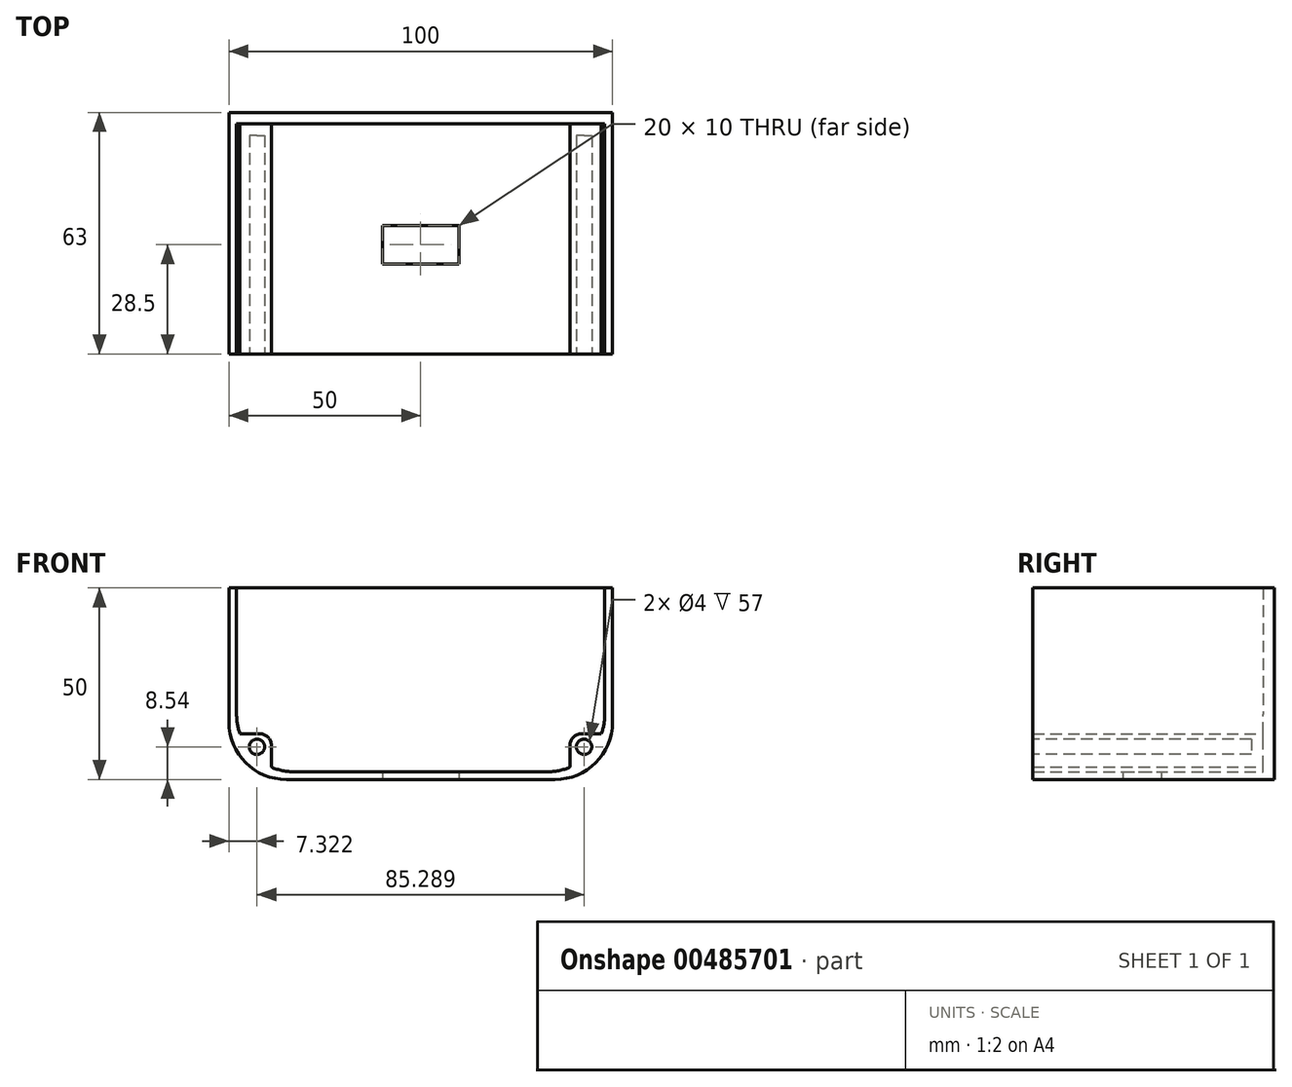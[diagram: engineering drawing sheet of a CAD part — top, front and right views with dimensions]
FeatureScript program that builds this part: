
annotation { "Feature Type Name" : "Feature", "Feature Type Description" : "" }
export const myFeature = defineFeature(function(context is Context, id is Id, definition is map)
    precondition{}
    {
        {
            var Q0;
            Q0=qCreatedBy(makeId("Front.planeOp"),FACE);
            var sketch = newSketch(context, id + "F0", { "sketchPlane" : qUnion([Q0])});
            skLineSegment(sketch, "E0.bottom", {"start": v(0, 0) * mm, "end": v(100, 0) * mm});
            skLineSegment(sketch, "E0.top", {"start": v(0, 50) * mm, "end": v(100, 50) * mm});
            skLineSegment(sketch, "E0.left", {"start": v(0, 0) * mm, "end": v(0, 50) * mm});
            skLineSegment(sketch, "E0.right", {"start": v(100, 0) * mm, "end": v(100, 50) * mm});
            skLineSegment(sketch, "E1.0", {"start": v(2, 2) * mm, "end": v(2, 48) * mm});
            skLineSegment(sketch, "E1.1", {"start": v(2, 2) * mm, "end": v(98, 2) * mm});
            skLineSegment(sketch, "E1.2", {"start": v(98, 2) * mm, "end": v(98, 48) * mm});
            skLineSegment(sketch, "E1.3", {"start": v(2, 48) * mm, "end": v(98, 48) * mm});
            skSolve(sketch);
        }
        {
            var Q0;
            Q0 = qSketchRegion(id + "F0", true);
            extrude(context, id + "F1", {"entities" : qUnion([Q0]), "depth" : 65 * mm, "offsetDistance" : 25 * mm});
        }
        {
            var Q0;
            Q0=makeQuery(id+"F1.opExtrude","CAP_FACE",FACE,{"disambiguationData":[OSD([sQuery(id+"F0.wireOp",EDGE,"E0.bottom"),sQuery(id+"F0.wireOp",EDGE,"E0.top"),sQuery(id+"F0.wireOp",EDGE,"E0.left"),sQuery(id+"F0.wireOp",EDGE,"E0.right"),sQuery(id+"F0.wireOp",EDGE,"E1.0"),sQuery(id+"F0.wireOp",EDGE,"E1.1"),sQuery(id+"F0.wireOp",EDGE,"E1.2"),sQuery(id+"F0.wireOp",EDGE,"E1.3")])],"isStart":false});
            var sketch = newSketch(context, id + "F2", { "sketchPlane" : qUnion([Q0])});
            skLineSegment(sketch, "E2.bottom", {"start": v(0, 0) * mm, "end": v(100, 0) * mm});
            skLineSegment(sketch, "E2.top", {"start": v(0, -8.6) * mm, "end": v(100, -8.6) * mm});
            skLineSegment(sketch, "E2.left", {"start": v(0, 0) * mm, "end": v(0, -8.6) * mm});
            skLineSegment(sketch, "E2.right", {"start": v(100, 0) * mm, "end": v(100, -8.6) * mm});
            skSolve(sketch);
        }
        {
            var Q0;
            Q0 = qSketchRegion(id + "F2", true);
            extrude(context, id + "F3", {"entities" : qUnion([Q0]), "operationType" : NewBodyOperationType.REMOVE, "oppositeDirection" : true, "depth" : 62.6 * mm, "offsetDistance" : 25 * mm});
        }
        {
            var Q0;
            Q0=makeQuery(id+"F1.opExtrude","CAP_FACE",FACE,{"disambiguationData":[OSD([sQuery(id+"F0.wireOp",EDGE,"E0.bottom"),sQuery(id+"F0.wireOp",EDGE,"E0.top"),sQuery(id+"F0.wireOp",EDGE,"E0.left"),sQuery(id+"F0.wireOp",EDGE,"E0.right"),sQuery(id+"F0.wireOp",EDGE,"E1.0"),sQuery(id+"F0.wireOp",EDGE,"E1.1"),sQuery(id+"F0.wireOp",EDGE,"E1.2"),sQuery(id+"F0.wireOp",EDGE,"E1.3")])],"isStart":true});
            var sketch = newSketch(context, id + "F4", { "sketchPlane" : qUnion([Q0])});
            skLineSegment(sketch, "E3.0.0", {"start": v(0, 50) * mm, "end": v(-100, 50) * mm});
            skLineSegment(sketch, "E3.0.1", {"start": v(-100, 50) * mm, "end": v(-100, 0) * mm});
            skLineSegment(sketch, "E3.0.2", {"start": v(-100, 0) * mm, "end": v(0, 0) * mm});
            skLineSegment(sketch, "E3.0.3", {"start": v(0, 0) * mm, "end": v(0, 50) * mm});
            skSolve(sketch);
        }
        {
            var Q0;
            Q0 = qSketchRegion(id + "F4", true);
            extrude(context, id + "F5", {"entities" : qUnion([Q0]), "operationType" : NewBodyOperationType.ADD, "oppositeDirection" : true, "depth" : 3 * mm, "offsetDistance" : 25 * mm});
        }
        {
            var Q0;
            Q0=makeQuery(id+"F5.opExtrude","CAP_FACE",FACE,{"disambiguationData":[OSD([sQuery(id+"F4.wireOp",EDGE,"E3.0.0"),sQuery(id+"F4.wireOp",EDGE,"E3.0.1"),sQuery(id+"F4.wireOp",EDGE,"E3.0.2"),sQuery(id+"F4.wireOp",EDGE,"E3.0.3")])],"isStart":false});
            var sketch = newSketch(context, id + "F6", { "sketchPlane" : qUnion([Q0])});
            skLineSegment(sketch, "E4.bottom", {"start": v(2, 2) * mm, "end": v(98, 2) * mm});
            skLineSegment(sketch, "E4.top", {"start": v(2, 55.98) * mm, "end": v(98, 55.98) * mm});
            skLineSegment(sketch, "E4.left", {"start": v(2, 55.98) * mm, "end": v(2, 2) * mm});
            skLineSegment(sketch, "E4.right", {"start": v(98, 55.98) * mm, "end": v(98, 2) * mm});
            skSolve(sketch);
        }
        {
            var Q0;
            Q0 = qSketchRegion(id + "F6", true);
            extrude(context, id + "F7", {"entities" : qUnion([Q0]), "operationType" : NewBodyOperationType.REMOVE, "depth" : 80.8 * mm, "offsetDistance" : 25 * mm});
        }
        {
            var Q0;
            Q0=makeQuery(id+"F1.opExtrude","CAP_FACE",FACE,{"disambiguationData":[OSD([sQuery(id+"F0.wireOp",EDGE,"E0.bottom"),sQuery(id+"F0.wireOp",EDGE,"E0.top"),sQuery(id+"F0.wireOp",EDGE,"E0.left"),sQuery(id+"F0.wireOp",EDGE,"E0.right"),sQuery(id+"F0.wireOp",EDGE,"E1.0"),sQuery(id+"F0.wireOp",EDGE,"E1.1"),sQuery(id+"F0.wireOp",EDGE,"E1.2"),sQuery(id+"F0.wireOp",EDGE,"E1.3")])],"isStart":false});
            var sketch = newSketch(context, id + "F8", { "sketchPlane" : qUnion([Q0])});
            skLineSegment(sketch, "E5.bottom", {"start": v(100, 0) * mm, "end": v(0, 0) * mm});
            skLineSegment(sketch, "E5.top", {"start": v(100, 100) * mm, "end": v(0, 100) * mm});
            skLineSegment(sketch, "E5.left", {"start": v(100, 0) * mm, "end": v(100, 100) * mm});
            skLineSegment(sketch, "E5.right", {"start": v(0, 0) * mm, "end": v(0, 100) * mm});
            skSolve(sketch);
        }
        {
            var Q0;
            Q0 = qSketchRegion(id + "F8", true);
            extrude(context, id + "F9", {"entities" : qUnion([Q0]), "operationType" : NewBodyOperationType.ADD, "oppositeDirection" : true, "depth" : 5 * mm, "offsetDistance" : 25 * mm});
        }
        {
            var Q0;
            Q0=makeQuery(id+"F9.boolean.opBoolean","MERGE",FACE,{"derivedFrom":[makeQuery(id+"F1.opExtrude","CAP_FACE",FACE,{"disambiguationData":[OSD([sQuery(id+"F0.wireOp",EDGE,"E0.bottom"),sQuery(id+"F0.wireOp",EDGE,"E0.top"),sQuery(id+"F0.wireOp",EDGE,"E0.left"),sQuery(id+"F0.wireOp",EDGE,"E0.right"),sQuery(id+"F0.wireOp",EDGE,"E1.0"),sQuery(id+"F0.wireOp",EDGE,"E1.1"),sQuery(id+"F0.wireOp",EDGE,"E1.2"),sQuery(id+"F0.wireOp",EDGE,"E1.3")])],"isStart":false}),makeQuery(id+"F9.opExtrude","CAP_FACE",FACE,{"disambiguationData":[OSD([sQuery(id+"F8.wireOp",EDGE,"E5.bottom"),sQuery(id+"F8.wireOp",EDGE,"E5.top"),sQuery(id+"F8.wireOp",EDGE,"E5.left"),sQuery(id+"F8.wireOp",EDGE,"E5.right")])],"isStart":true})]});
            var sketch = newSketch(context, id + "F10", { "sketchPlane" : qUnion([Q0])});
            skLineSegment(sketch, "E6.bottom", {"start": v(131.94, -36.62) * mm, "end": v(-47.05, -36.62) * mm});
            skLineSegment(sketch, "E6.top", {"start": v(131.94, 135.28) * mm, "end": v(-47.05, 135.28) * mm});
            skLineSegment(sketch, "E6.left", {"start": v(131.94, -36.62) * mm, "end": v(131.94, 135.28) * mm});
            skLineSegment(sketch, "E6.right", {"start": v(-47.05, -36.62) * mm, "end": v(-47.05, 135.28) * mm});
            skSolve(sketch);
        }
        {
            var Q0;
            Q0 = qSketchRegion(id + "F10", true);
            extrude(context, id + "F11", {"entities" : qUnion([Q0]), "operationType" : NewBodyOperationType.REMOVE, "oppositeDirection" : true, "depth" : 2 * mm, "offsetDistance" : 25 * mm});
        }
        {
            var Q0;
            Q0=makeQuery(id+"F1.opExtrude","SWEPT_FACE",FACE,{"disambiguationData":[OSD([sQuery(id+"F0.wireOp",EDGE,"E0.bottom")])]});
            var sketch = newSketch(context, id + "F12", { "sketchPlane" : qUnion([Q0])});
            skLineSegment(sketch, "E7.bottom", {"start": v(40, 26.5) * mm, "end": v(60, 26.5) * mm});
            skLineSegment(sketch, "E7.top", {"start": v(40, 36.5) * mm, "end": v(60, 36.5) * mm});
            skLineSegment(sketch, "E7.left", {"start": v(40, 26.5) * mm, "end": v(40, 36.5) * mm});
            skLineSegment(sketch, "E7.right", {"start": v(60, 26.5) * mm, "end": v(60, 36.5) * mm});
            skPoint(sketch, "E7.middle", {"position": v(50, 31.5) * mm});
            skPoint(sketch, "E7.middle.positionSnap0", {"position": v(0, 31.5) * mm});
            skPoint(sketch, "E7.middle.positionSnap1", {"position": v(50, 0) * mm});
            skPoint(sketch, "E7.centerSnap0", {"position": v(0, 31.5) * mm});
            skPoint(sketch, "E7.centerSnap1", {"position": v(50, 0) * mm});
            skSolve(sketch);
        }
        {
            var Q0;
            Q0 = qSketchRegion(id + "F12", true);
            extrude(context, id + "F13", {"entities" : qUnion([Q0]), "operationType" : NewBodyOperationType.REMOVE, "oppositeDirection" : true, "depth" : 25 * mm, "offsetDistance" : 25 * mm});
        }
        {
            var Q0;
            Q0=makeQuery(id+"F11.boolean.opBoolean","COPY",FACE,{"derivedFrom":makeQuery(id+"F11.opExtrude","CAP_FACE",FACE,{"disambiguationData":[OSD([sQuery(id+"F10.wireOp",EDGE,"E6.bottom"),sQuery(id+"F10.wireOp",EDGE,"E6.top"),sQuery(id+"F10.wireOp",EDGE,"E6.left"),sQuery(id+"F10.wireOp",EDGE,"E6.right")])],"isStart":false})});
            var sketch = newSketch(context, id + "F14", { "sketchPlane" : qUnion([Q0])});
            skCircle(sketch, "E8", {"center": v(105.67, 65.55) * mm, "radius": 2.2 * mm});
            skArc(sketch, "E9", {"start": v(105.34, 60.56) * mm, "mid": v(110.66, 65.38) * mm, "end": v(105.68, 70.55) * mm});
            skLineSegment(sketch, "E10", {"start": v(106, 60.56) * mm, "end": v(100, 60.56) * mm});
            skLineSegment(sketch, "E11", {"start": v(100, 60.56) * mm, "end": v(100, 70.56) * mm});
            skLineSegment(sketch, "E12", {"start": v(100, 70.56) * mm, "end": v(105.68, 70.55) * mm});
            skLineSegment(sketch, "E13", {"start": v(50, 0) * mm, "end": v(50, 14.7) * mm, "construction": true});
            skLineSegment(sketch, "E14.MirrorCS", {"start": v(0, 60.56) * mm, "end": v(0, 70.56) * mm});
            skLineSegment(sketch, "E15.MirrorCS", {"start": v(0, 70.56) * mm, "end": v(-5.68, 70.55) * mm});
            skLineSegment(sketch, "E16.MirrorCS", {"start": v(-6, 60.56) * mm, "end": v(0, 60.56) * mm});
            skCircle(sketch, "E17.MirrorC", {"center": v(-5.67, 65.55) * mm, "radius": 2.2 * mm});
            skArc(sketch, "E18.MirrorC", {"start": v(-5.34, 60.56) * mm, "mid": v(-10.66, 65.38) * mm, "end": v(-5.68, 70.55) * mm});
            skSolve(sketch);
        }
        {
            var Q0;
            Q0 = qSketchRegion(id + "F14", true);
            extrude(context, id + "F15", {"entities" : qUnion([Q0]), "operationType" : NewBodyOperationType.ADD, "oppositeDirection" : true, "depth" : 3 * mm, "offsetDistance" : 25 * mm});
        }
        {
            var Q0;
            Q0=makeQuery(id+"F15.opExtrude","SWEPT_EDGE",EDGE,{"disambiguationData":[OSD([sQuery(id+"F0.wireOp",EDGE,"E0.right"),sQuery(id+"F8.wireOp",EDGE,"E5.left"),sQuery(id+"F10.wireOp",EDGE,"E6.bottom"),sQuery(id+"F10.wireOp",EDGE,"E6.top"),sQuery(id+"F10.wireOp",EDGE,"E6.left"),sQuery(id+"F10.wireOp",EDGE,"E6.right"),sQuery(id+"F14.wireOp",EDGE,"E10"),sQuery(id+"F14.wireOp",EDGE,"E11")])]});
            var Q1;
            Q1=makeQuery(id+"F15.opExtrude","SWEPT_EDGE",EDGE,{"disambiguationData":[OSD([sQuery(id+"F0.wireOp",EDGE,"E0.right"),sQuery(id+"F8.wireOp",EDGE,"E5.left"),sQuery(id+"F10.wireOp",EDGE,"E6.bottom"),sQuery(id+"F10.wireOp",EDGE,"E6.top"),sQuery(id+"F10.wireOp",EDGE,"E6.left"),sQuery(id+"F10.wireOp",EDGE,"E6.right"),sQuery(id+"F14.wireOp",EDGE,"E11"),sQuery(id+"F14.wireOp",EDGE,"E12")])]});
            var Q2;
            Q2=makeQuery(id+"F15.opExtrude","SWEPT_EDGE",EDGE,{"disambiguationData":[OSD([sQuery(id+"F0.wireOp",EDGE,"E0.left"),sQuery(id+"F8.wireOp",EDGE,"E5.right"),sQuery(id+"F10.wireOp",EDGE,"E6.bottom"),sQuery(id+"F10.wireOp",EDGE,"E6.top"),sQuery(id+"F10.wireOp",EDGE,"E6.left"),sQuery(id+"F10.wireOp",EDGE,"E6.right"),sQuery(id+"F14.wireOp",EDGE,"E14.MirrorCS"),sQuery(id+"F14.wireOp",EDGE,"E16.MirrorCS")])]});
            var Q3;
            Q3=makeQuery(id+"F15.opExtrude","SWEPT_EDGE",EDGE,{"disambiguationData":[OSD([sQuery(id+"F0.wireOp",EDGE,"E0.left"),sQuery(id+"F8.wireOp",EDGE,"E5.right"),sQuery(id+"F10.wireOp",EDGE,"E6.bottom"),sQuery(id+"F10.wireOp",EDGE,"E6.top"),sQuery(id+"F10.wireOp",EDGE,"E6.left"),sQuery(id+"F10.wireOp",EDGE,"E6.right"),sQuery(id+"F14.wireOp",EDGE,"E14.MirrorCS"),sQuery(id+"F14.wireOp",EDGE,"E15.MirrorCS")])]});
            fillet(context, id + "F16", {"entities" : qUnion([Q0, Q1, Q2, Q3]), "radius" : 5 * mm, "tangentPropagation" : true, "allowEdgeOverflow" : false});
        }
        {
            var Q0;
            Q0=makeQuery(id+"F1.opExtrude","SWEPT_EDGE",EDGE,{"disambiguationData":[OSD([sQuery(id+"F0.wireOp",EDGE,"E1.1"),sQuery(id+"F0.wireOp",EDGE,"E1.2")])]});
            var Q1;
            Q1=makeQuery(id+"F1.opExtrude","SWEPT_EDGE",EDGE,{"disambiguationData":[OSD([sQuery(id+"F0.wireOp",EDGE,"E1.0"),sQuery(id+"F0.wireOp",EDGE,"E1.1")])]});
            var Q2;
            Q2=makeQuery(id+"F1.opExtrude","SWEPT_EDGE",EDGE,{"disambiguationData":[OSD([sQuery(id+"F0.wireOp",EDGE,"E0.bottom"),sQuery(id+"F0.wireOp",EDGE,"E0.right")])]});
            var Q3;
            Q3=makeQuery(id+"F1.opExtrude","SWEPT_EDGE",EDGE,{"disambiguationData":[OSD([sQuery(id+"F0.wireOp",EDGE,"E0.bottom"),sQuery(id+"F0.wireOp",EDGE,"E0.left")])]});
            fillet(context, id + "F17", {"entities" : qUnion([Q0, Q1, Q2, Q3]), "radius" : 15 * mm, "tangentPropagation" : true, "allowEdgeOverflow" : false});
        }
        {
            var Q0;
            Q0=makeQuery(id+"F15.boolean.opBoolean","MERGE",FACE,{"derivedFrom":[makeQuery(id+"F11.boolean.opBoolean","COPY",FACE,{"derivedFrom":makeQuery(id+"F11.opExtrude","CAP_FACE",FACE,{"disambiguationData":[OSD([sQuery(id+"F10.wireOp",EDGE,"E6.bottom"),sQuery(id+"F10.wireOp",EDGE,"E6.top"),sQuery(id+"F10.wireOp",EDGE,"E6.left"),sQuery(id+"F10.wireOp",EDGE,"E6.right")])],"isStart":false})}),makeQuery(id+"F15.opExtrude","CAP_FACE",FACE,{"disambiguationData":[OSD([sQuery(id+"F14.wireOp",EDGE,"E8"),sQuery(id+"F14.wireOp",EDGE,"E9"),sQuery(id+"F14.wireOp",EDGE,"E10"),sQuery(id+"F14.wireOp",EDGE,"E11"),sQuery(id+"F14.wireOp",EDGE,"E12")])],"isStart":true}),makeQuery(id+"F15.opExtrude","CAP_FACE",FACE,{"disambiguationData":[OSD([sQuery(id+"F14.wireOp",EDGE,"E14.MirrorCS"),sQuery(id+"F14.wireOp",EDGE,"E15.MirrorCS"),sQuery(id+"F14.wireOp",EDGE,"E16.MirrorCS"),sQuery(id+"F14.wireOp",EDGE,"E17.MirrorC"),sQuery(id+"F14.wireOp",EDGE,"E18.MirrorC")])],"isStart":true})]});
            var sketch = newSketch(context, id + "F18", { "sketchPlane" : qUnion([Q0])});
            skCircle(sketch, "E19", {"center": v(85, 15) * mm, "radius": 1.5 * mm});
            skCircle(sketch, "E20.0.1.0", {"center": v(85, 23) * mm, "radius": 1.5 * mm});
            skCircle(sketch, "E20.0.2.0", {"center": v(85, 31) * mm, "radius": 1.5 * mm});
            skCircle(sketch, "E20.0.3.0", {"center": v(85, 39) * mm, "radius": 1.5 * mm});
            skCircle(sketch, "E20.0.4.0", {"center": v(85, 47) * mm, "radius": 1.5 * mm});
            skCircle(sketch, "E20.1.0.0", {"center": v(77, 15) * mm, "radius": 1.5 * mm});
            skCircle(sketch, "E20.1.1.0", {"center": v(77, 23) * mm, "radius": 1.5 * mm});
            skCircle(sketch, "E20.1.2.0", {"center": v(77, 31) * mm, "radius": 1.5 * mm});
            skCircle(sketch, "E20.1.3.0", {"center": v(77, 39) * mm, "radius": 1.5 * mm});
            skCircle(sketch, "E20.1.4.0", {"center": v(77, 47) * mm, "radius": 1.5 * mm});
            skCircle(sketch, "E20.2.0.0", {"center": v(69, 15) * mm, "radius": 1.5 * mm});
            skCircle(sketch, "E20.2.1.0", {"center": v(69, 23) * mm, "radius": 1.5 * mm});
            skCircle(sketch, "E20.2.2.0", {"center": v(69, 31) * mm, "radius": 1.5 * mm});
            skCircle(sketch, "E20.2.3.0", {"center": v(69, 39) * mm, "radius": 1.5 * mm});
            skCircle(sketch, "E20.2.4.0", {"center": v(69, 47) * mm, "radius": 1.5 * mm});
            skCircle(sketch, "E20.3.0.0", {"center": v(61, 15) * mm, "radius": 1.5 * mm});
            skCircle(sketch, "E20.3.1.0", {"center": v(61, 23) * mm, "radius": 1.5 * mm});
            skCircle(sketch, "E20.3.2.0", {"center": v(61, 31) * mm, "radius": 1.5 * mm});
            skCircle(sketch, "E20.3.3.0", {"center": v(61, 39) * mm, "radius": 1.5 * mm});
            skCircle(sketch, "E20.3.4.0", {"center": v(61, 47) * mm, "radius": 1.5 * mm});
            skCircle(sketch, "E20.4.0.0", {"center": v(53, 15) * mm, "radius": 1.5 * mm});
            skCircle(sketch, "E20.4.1.0", {"center": v(53, 23) * mm, "radius": 1.5 * mm});
            skCircle(sketch, "E20.4.2.0", {"center": v(53, 31) * mm, "radius": 1.5 * mm});
            skCircle(sketch, "E20.4.3.0", {"center": v(53, 39) * mm, "radius": 1.5 * mm});
            skCircle(sketch, "E20.4.4.0", {"center": v(53, 47) * mm, "radius": 1.5 * mm});
            skCircle(sketch, "E20.5.0.0", {"center": v(45, 15) * mm, "radius": 1.5 * mm});
            skCircle(sketch, "E20.5.1.0", {"center": v(45, 23) * mm, "radius": 1.5 * mm});
            skCircle(sketch, "E20.5.2.0", {"center": v(45, 31) * mm, "radius": 1.5 * mm});
            skCircle(sketch, "E20.5.3.0", {"center": v(45, 39) * mm, "radius": 1.5 * mm});
            skCircle(sketch, "E20.5.4.0", {"center": v(45, 47) * mm, "radius": 1.5 * mm});
            skCircle(sketch, "E20.6.0.0", {"center": v(37, 15) * mm, "radius": 1.5 * mm});
            skCircle(sketch, "E20.6.1.0", {"center": v(37, 23) * mm, "radius": 1.5 * mm});
            skCircle(sketch, "E20.6.2.0", {"center": v(37, 31) * mm, "radius": 1.5 * mm});
            skCircle(sketch, "E20.6.3.0", {"center": v(37, 39) * mm, "radius": 1.5 * mm});
            skCircle(sketch, "E20.6.4.0", {"center": v(37, 47) * mm, "radius": 1.5 * mm});
            skCircle(sketch, "E20.7.0.0", {"center": v(29, 15) * mm, "radius": 1.5 * mm});
            skCircle(sketch, "E20.7.1.0", {"center": v(29, 23) * mm, "radius": 1.5 * mm});
            skCircle(sketch, "E20.7.2.0", {"center": v(29, 31) * mm, "radius": 1.5 * mm});
            skCircle(sketch, "E20.7.3.0", {"center": v(29, 39) * mm, "radius": 1.5 * mm});
            skCircle(sketch, "E20.7.4.0", {"center": v(29, 47) * mm, "radius": 1.5 * mm});
            skCircle(sketch, "E20.8.0.0", {"center": v(21, 15) * mm, "radius": 1.5 * mm});
            skCircle(sketch, "E20.8.1.0", {"center": v(21, 23) * mm, "radius": 1.5 * mm});
            skCircle(sketch, "E20.8.2.0", {"center": v(21, 31) * mm, "radius": 1.5 * mm});
            skCircle(sketch, "E20.8.3.0", {"center": v(21, 39) * mm, "radius": 1.5 * mm});
            skCircle(sketch, "E20.8.4.0", {"center": v(21, 47) * mm, "radius": 1.5 * mm});
            skCircle(sketch, "E20.9.0.0", {"center": v(13, 15) * mm, "radius": 1.5 * mm});
            skCircle(sketch, "E20.9.1.0", {"center": v(13, 23) * mm, "radius": 1.5 * mm});
            skCircle(sketch, "E20.9.2.0", {"center": v(13, 31) * mm, "radius": 1.5 * mm});
            skCircle(sketch, "E20.9.3.0", {"center": v(13, 39) * mm, "radius": 1.5 * mm});
            skCircle(sketch, "E20.9.4.0", {"center": v(13, 47) * mm, "radius": 1.5 * mm});
            skLineSegment(sketch, "E20.direction1", {"start": v(85, 15) * mm, "end": v(77, 15) * mm, "construction": true});
            skLineSegment(sketch, "E20.direction2", {"start": v(85, 15) * mm, "end": v(85, 23) * mm, "construction": true});
            skSolve(sketch);
        }
        {
            var Q0;
            Q0 = qSketchRegion(id + "F18", true);
            extrude(context, id + "F19", {"entities" : qUnion([Q0]), "operationType" : NewBodyOperationType.REMOVE, "oppositeDirection" : true, "depth" : 25 * mm, "offsetDistance" : 25 * mm});
        }
        {
            var Q0;
            {var subQ5=sQuery(id+"F0.wireOp",EDGE,"E0.bottom");var subQ11=sQuery(id+"F8.wireOp",EDGE,"E5.right");var subQ12=sQuery(id+"F0.wireOp",EDGE,"E0.left");Q0=makeQuery(id+"F15.boolean.opBoolean","SPLIT",FACE,{"disambiguationData":[TD([makeQuery(id+"F1.opExtrude","SWEPT_FACE",FACE,{"disambiguationData":[OSD([subQ5])]})])],"derivedFrom":makeQuery(id+"F9.boolean.opBoolean","MERGE",FACE,{"derivedFrom":[makeQuery(id+"F1.opExtrude","SWEPT_FACE",FACE,{"disambiguationData":[OSD([subQ12])]}),makeQuery(id+"F9.opExtrude","SWEPT_FACE",FACE,{"disambiguationData":[OSD([subQ11])]})]})});}
            var sketch = newSketch(context, id + "F20", { "sketchPlane" : qUnion([Q0])});
            skLineSegment(sketch, "E21.bottom", {"start": v(60, 100) * mm, "end": v(78.03, 100) * mm});
            skLineSegment(sketch, "E21.top", {"start": v(60, -17.16) * mm, "end": v(78.03, -17.16) * mm});
            skLineSegment(sketch, "E21.left", {"start": v(60, 100) * mm, "end": v(60, -17.16) * mm});
            skLineSegment(sketch, "E21.right", {"start": v(78.03, 100) * mm, "end": v(78.03, -17.16) * mm});
            skSolve(sketch);
        }
        {
            var Q0;
            Q0 = qSketchRegion(id + "F20", true);
            extrude(context, id + "F21", {"entities" : qUnion([Q0]), "operationType" : NewBodyOperationType.REMOVE, "oppositeDirection" : true, "depth" : 124.6 * mm, "offsetDistance" : 25 * mm, "hasSecondDirection" : true, "secondDirectionOppositeDirection" : false, "secondDirectionDepth" : 25 * mm});
        }
        {
            var Q0;
            Q0=makeQuery(id+"F7.boolean.opBoolean","MERGE",FACE,{"derivedFrom":[makeQuery(id+"F5.opExtrude","CAP_FACE",FACE,{"disambiguationData":[OSD([sQuery(id+"F4.wireOp",EDGE,"E3.0.0"),sQuery(id+"F4.wireOp",EDGE,"E3.0.1"),sQuery(id+"F4.wireOp",EDGE,"E3.0.2"),sQuery(id+"F4.wireOp",EDGE,"E3.0.3")])],"isStart":false}),makeQuery(id+"F7.opExtrude","CAP_FACE",FACE,{"disambiguationData":[OSD([sQuery(id+"F6.wireOp",EDGE,"E4.bottom"),sQuery(id+"F6.wireOp",EDGE,"E4.top"),sQuery(id+"F6.wireOp",EDGE,"E4.left"),sQuery(id+"F6.wireOp",EDGE,"E4.right")])],"isStart":true})]});
            var sketch = newSketch(context, id + "F22", { "sketchPlane" : qUnion([Q0])});
            skLineSegment(sketch, "E22", {"start": v(88.94, 3.23) * mm, "end": v(88.94, 11.91) * mm});
            skLineSegment(sketch, "E23", {"start": v(88.94, 11.91) * mm, "end": v(97.11, 11.91) * mm});
            skLineSegment(sketch, "E24", {"start": v(97.11, 11.91) * mm, "end": v(97.11, 6.17) * mm});
            skLineSegment(sketch, "E25", {"start": v(97.11, 6.17) * mm, "end": v(88.94, 3.23) * mm});
            skLineSegment(sketch, "E26", {"start": v(50, 0) * mm, "end": v(50, 9.4) * mm, "construction": true});
            skPoint(sketch, "E26.startSnap0", {"position": v(50, 2) * mm});
            skLineSegment(sketch, "E27.MirrorCS", {"start": v(2.89, 6.17) * mm, "end": v(11.06, 3.23) * mm});
            skLineSegment(sketch, "E28.MirrorCS", {"start": v(11.06, 11.91) * mm, "end": v(2.89, 11.91) * mm});
            skLineSegment(sketch, "E29.MirrorCS", {"start": v(11.06, 3.23) * mm, "end": v(11.06, 11.91) * mm});
            skLineSegment(sketch, "E30.MirrorCS", {"start": v(2.89, 11.91) * mm, "end": v(2.89, 6.17) * mm});
            skSolve(sketch);
        }
        {
            var Q0;
            Q0 = qSketchRegion(id + "F22", true);
            var Q1;
            Q1=makeQuery(id+"F21.boolean.opBoolean","COPY",FACE,{"derivedFrom":makeQuery(id+"F21.opExtrude","SWEPT_FACE",FACE,{"disambiguationData":[OSD([sQuery(id+"F20.wireOp",EDGE,"E21.left")])]})});
            extrude(context, id + "F23", {"entities" : qUnion([Q0]), "operationType" : NewBodyOperationType.ADD, "endBound" : BoundingType.UP_TO_SURFACE, "depth" : 25 * mm, "endBoundEntityFace" : qUnion([Q1]), "offsetDistance" : 25 * mm});
        }
        {
            var Q0;
            {var subQ0=sQuery(id+"F20.wireOp",EDGE,"E21.left");Q0=makeQuery(id+"F23.boolean.opBoolean","MERGE",FACE,{"derivedFrom":[makeQuery(id+"F21.boolean.opBoolean","COPY",FACE,{"derivedFrom":makeQuery(id+"F21.opExtrude","SWEPT_FACE",FACE,{"disambiguationData":[OSD([subQ0])]})}),makeQuery(id+"F23.opExtrude","CAP_FACE",FACE,{"disambiguationData":[OSD([subQ0]),OD(0.0)],"isStart":false}),makeQuery(id+"F23.opExtrude","CAP_FACE",FACE,{"disambiguationData":[OSD([subQ0]),OD(1.0)],"isStart":false})]});}
            var sketch = newSketch(context, id + "F24", { "sketchPlane" : qUnion([Q0])});
            skCircle(sketch, "E31.0", {"center": v(92.61, 8.54) * mm, "radius": 2 * mm});
            skCircle(sketch, "E32.0", {"center": v(7.32, 8.54) * mm, "radius": 2 * mm});
            skSolve(sketch);
        }
        {
            var Q0;
            Q0 = qSketchRegion(id + "F24", true);
            var Q1;
            {var subQ1=sQuery(id+"F6.wireOp",EDGE,"E4.right");var subQ3=sQuery(id+"F0.wireOp",EDGE,"E1.0");var subQ4=sQuery(id+"F6.wireOp",EDGE,"E4.left");Q1=makeQuery(id+"F23.boolean.opBoolean","SPLIT",FACE,{"disambiguationData":[TD([makeQuery(id+"F1.opExtrude","SWEPT_FACE",FACE,{"disambiguationData":[OSD([subQ3])]})])],"derivedFrom":makeQuery(id+"F7.boolean.opBoolean","MERGE",FACE,{"derivedFrom":[makeQuery(id+"F5.opExtrude","CAP_FACE",FACE,{"disambiguationData":[OSD([sQuery(id+"F4.wireOp",EDGE,"E3.0.0"),sQuery(id+"F4.wireOp",EDGE,"E3.0.1"),sQuery(id+"F4.wireOp",EDGE,"E3.0.2"),sQuery(id+"F4.wireOp",EDGE,"E3.0.3")])],"isStart":false}),makeQuery(id+"F7.opExtrude","CAP_FACE",FACE,{"disambiguationData":[OSD([sQuery(id+"F6.wireOp",EDGE,"E4.bottom"),sQuery(id+"F6.wireOp",EDGE,"E4.top"),subQ4,subQ1])],"isStart":true})]})});}
            extrude(context, id + "F25", {"entities" : qUnion([Q0]), "operationType" : NewBodyOperationType.REMOVE, "endBound" : BoundingType.UP_TO_SURFACE, "oppositeDirection" : true, "depth" : 25 * mm, "endBoundEntityFace" : qUnion([Q1]), "offsetDistance" : 25 * mm});
        }
        {
            var Q0;
            Q0=makeQuery(id+"F5.boolean.opBoolean","MERGE",FACE,{"derivedFrom":[makeQuery(id+"F1.opExtrude","CAP_FACE",FACE,{"disambiguationData":[OSD([sQuery(id+"F0.wireOp",EDGE,"E0.bottom"),sQuery(id+"F0.wireOp",EDGE,"E0.top"),sQuery(id+"F0.wireOp",EDGE,"E0.left"),sQuery(id+"F0.wireOp",EDGE,"E0.right"),sQuery(id+"F0.wireOp",EDGE,"E1.0"),sQuery(id+"F0.wireOp",EDGE,"E1.1"),sQuery(id+"F0.wireOp",EDGE,"E1.2"),sQuery(id+"F0.wireOp",EDGE,"E1.3")])],"isStart":true}),makeQuery(id+"F5.opExtrude","CAP_FACE",FACE,{"disambiguationData":[OSD([sQuery(id+"F4.wireOp",EDGE,"E3.0.0"),sQuery(id+"F4.wireOp",EDGE,"E3.0.1"),sQuery(id+"F4.wireOp",EDGE,"E3.0.2"),sQuery(id+"F4.wireOp",EDGE,"E3.0.3")])],"isStart":true})]});
            var sketch = newSketch(context, id + "F26", { "sketchPlane" : qUnion([Q0])});
            skLineSegment(sketch, "E33.0.0", {"start": v(-85, 0) * mm, "end": v(-15, 0) * mm});
            skArc(sketch, "E33.0.1", {"start": v(-15, 0) * mm, "mid": v(-4.4, 4.4) * mm, "end": v(0, 15) * mm});
            skLineSegment(sketch, "E33.0.2", {"start": v(0, 15) * mm, "end": v(0, 50) * mm});
            skLineSegment(sketch, "E33.0.3", {"start": v(0, 50) * mm, "end": v(-100, 50) * mm});
            skLineSegment(sketch, "E33.0.4", {"start": v(-100, 50) * mm, "end": v(-100, 15) * mm});
            skArc(sketch, "E33.0.5", {"start": v(-100, 15) * mm, "mid": v(-95.6, 4.4) * mm, "end": v(-85, 0) * mm});
            skSolve(sketch);
        }
        {
            var Q0;
            Q0 = qSketchRegion(id + "F26", true);
            extrude(context, id + "F27", {"entities" : qUnion([Q0]), "operationType" : NewBodyOperationType.ADD, "depth" : 3 * mm, "offsetDistance" : 25 * mm});
        }
        {
            var Q0;
            Q0=makeQuery(id+"F7.boolean.opBoolean","MERGE",FACE,{"derivedFrom":[makeQuery(id+"F5.opExtrude","CAP_FACE",FACE,{"disambiguationData":[OSD([sQuery(id+"F4.wireOp",EDGE,"E3.0.0"),sQuery(id+"F4.wireOp",EDGE,"E3.0.1"),sQuery(id+"F4.wireOp",EDGE,"E3.0.2"),sQuery(id+"F4.wireOp",EDGE,"E3.0.3")])],"isStart":false}),makeQuery(id+"F7.opExtrude","CAP_FACE",FACE,{"disambiguationData":[OSD([sQuery(id+"F6.wireOp",EDGE,"E4.bottom"),sQuery(id+"F6.wireOp",EDGE,"E4.top"),sQuery(id+"F6.wireOp",EDGE,"E4.left"),sQuery(id+"F6.wireOp",EDGE,"E4.right")])],"isStart":true})]});
            var sketch = newSketch(context, id + "F28", { "sketchPlane" : qUnion([Q0])});
            skLineSegment(sketch, "E34.0.0", {"start": v(2.89, 11.91) * mm, "end": v(11.06, 11.91) * mm});
            skLineSegment(sketch, "E34.0.1", {"start": v(11.06, 11.91) * mm, "end": v(11.06, 3.23) * mm});
            skArc(sketch, "E34.0.2", {"start": v(11.06, 3.23) * mm, "mid": v(13.97, 2.3) * mm, "end": v(17, 2) * mm});
            skLineSegment(sketch, "E34.0.3", {"start": v(17, 2) * mm, "end": v(83, 2) * mm});
            skArc(sketch, "E34.0.4", {"start": v(83, 2) * mm, "mid": v(86.03, 2.3) * mm, "end": v(88.94, 3.23) * mm});
            skLineSegment(sketch, "E34.0.5", {"start": v(88.94, 3.23) * mm, "end": v(88.94, 11.91) * mm});
            skLineSegment(sketch, "E34.0.6", {"start": v(88.94, 11.91) * mm, "end": v(97.11, 11.91) * mm});
            skArc(sketch, "E34.0.7", {"start": v(97.11, 11.91) * mm, "mid": v(97.78, 14.42) * mm, "end": v(98, 17) * mm});
            skLineSegment(sketch, "E34.0.8", {"start": v(98, 17) * mm, "end": v(98, 50) * mm});
            skLineSegment(sketch, "E34.0.9", {"start": v(98, 50) * mm, "end": v(2, 50) * mm});
            skLineSegment(sketch, "E34.0.10", {"start": v(2, 50) * mm, "end": v(2, 17) * mm});
            skArc(sketch, "E34.0.11", {"start": v(2, 17) * mm, "mid": v(2.22, 14.42) * mm, "end": v(2.89, 11.91) * mm});
            skSolve(sketch);
        }
        {
            var Q0;
            Q0 = qSketchRegion(id + "F28", true);
            extrude(context, id + "F29", {"entities" : qUnion([Q0]), "operationType" : NewBodyOperationType.REMOVE, "oppositeDirection" : true, "depth" : 3 * mm, "offsetDistance" : 25 * mm});
        }
        {
            var Q0;
            Q0=makeQuery(id+"F29.boolean.opBoolean","MERGE",EDGE,{"derivedFrom":[makeQuery(id+"F23.opExtrude","SWEPT_EDGE",EDGE,{"disambiguationData":[OSD([sQuery(id+"F22.wireOp",EDGE,"E22"),sQuery(id+"F22.wireOp",EDGE,"E23")])]}),makeQuery(id+"F29.opExtrude","SWEPT_EDGE",EDGE,{"disambiguationData":[OSD([sQuery(id+"F28.wireOp",EDGE,"E34.0.5"),sQuery(id+"F28.wireOp",EDGE,"E34.0.6")])]})]});
            var Q1;
            Q1=makeQuery(id+"F29.boolean.opBoolean","MERGE",EDGE,{"derivedFrom":[makeQuery(id+"F23.opExtrude","SWEPT_EDGE",EDGE,{"disambiguationData":[OSD([sQuery(id+"F22.wireOp",EDGE,"E28.MirrorCS"),sQuery(id+"F22.wireOp",EDGE,"E29.MirrorCS")])]}),makeQuery(id+"F29.opExtrude","SWEPT_EDGE",EDGE,{"disambiguationData":[OSD([sQuery(id+"F28.wireOp",EDGE,"E34.0.0"),sQuery(id+"F28.wireOp",EDGE,"E34.0.1")])]})]});
            fillet(context, id + "F30", {"entities" : qUnion([Q0, Q1]), "radius" : 3 * mm, "tangentPropagation" : true, "allowEdgeOverflow" : false});
        }
    });
